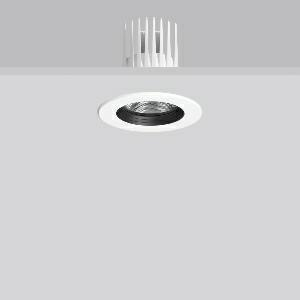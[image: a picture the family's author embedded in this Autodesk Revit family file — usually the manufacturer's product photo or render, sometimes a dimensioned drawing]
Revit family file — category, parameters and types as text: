
# Revit family: heledon_mini_e_901741_002_76_57f9
name_source: partatom
category: Lighting Fixtures
units: mm (PartAtom-declared; Revit-internal decimal feet)

## family parameters
Cut with Voids When Loaded = No
Host = Face
Light Source = No
Part Type = Normal
Room Calculation Point = No
Round Connector Dimension = Use Diameter
Shared = No

## types (1)
- HELEDON mini E (1 x LED Modul 930, 2450 lm, 3000)
    Apparent Load = 20 VA
    Approval mark = CE
    CIE Flux Codes = 99 100 100 100 100
    Color Rendering = 90
    Color Temperature = 3000
    Default Elevation = 1800 mm
    Description = Series: HELEDON mini
Round recessed downlight. Housing: die-cast aluminium, powder-coated. Black plastic ring and recessed LED to prevent glare from the side. Optical assembly with reflector made of MIRO-Silver with 98% total light reflection for outstanding efficiency - can be changed without tools. Best colour rendering index Ra>90. Suitable for Recessed ceiling mounting. Installation without tools thanks to spring fastening system. Including separate LED converter with connecting cable 600 mm.High quality converter without flickering and stroboscopic effect. Through-wiring box (5 pole) available as accessory. The following accessories can be mounted without use of tools: interchangeable lenses, decorative glasses, honeycomb louvre, clear and frosted diffusers, white interchangeable plastic ring. 
Colour: traffic white, matt (RAL 9016)
Diameter: 124 mm
Height: 3 mm
Cut-out diameter: 114 mm
Recess height: 170 mm
Luminaire: recess height: 120 mm
Lamp: LED
Socket: without socket
Colour temperature: 3000K
Colour rendering index (CRI): 92
System power: 20 W
Rated luminous flux: 2450 lm
Luminous efficiency: 123 lm/W
Control gear: Converter, dimmable, DALI
Protection class: II
Type of protection: IP 20
    Height = 0 mm  [stored 0 ft]
    Lamp = 1 x LED Modul 930
    Lamp Light Flux = 2450 lm
    Lamp count = 1
    Length = 124 mm  [stored 0.406824 ft]
    Lifetime = 50000 h
    Luminous efficacy = 123 lm/W
    Manufacturer = RZB
    ModVariant = No
    Model = 901741.002.76
    Mounting Place = Ceiling
    Mounting Type = Recessed
    Number of Poles = 1
    OnlyDefault = Yes
    Power Factor = 1
    Product Name = HELEDON mini E
    Product group = Recessed downlights
    ProductGroupID = 402
    Protection Class = Protection class II
    Protection Degree = IP 20
    RLX_Detail_Level = 1
    RLX_Emergency_Light_Flux = 0 lm
    RLX_Emergency_Type = 0
    RLX_Emergency_Type_DB = No
    RlxData = <blob elided: 126401 chars, md5=0d5689f4>
    Socket = socket
    Standby Power = 0 W
    System Light Flux = 2450 lm
    System Power = 20 W
    Type Comments = Product without accessories
    Type Image = 901657.002.jpg
    URL = http://relux.com
    VarID = ---
    Voltage = 230 V
    Voltage Range = 220-240 V
    Weight = 0.00 kg
    Width = 0 mm  [stored 0 ft]

note: [stored X ft] marks values corroborated as IEEE doubles in the binary element streams (Revit-internal decimal feet)

## geometry (parser evidence)
native form markers: Blend x4, Sweep x12
no freeform markers — native parametric forms only
